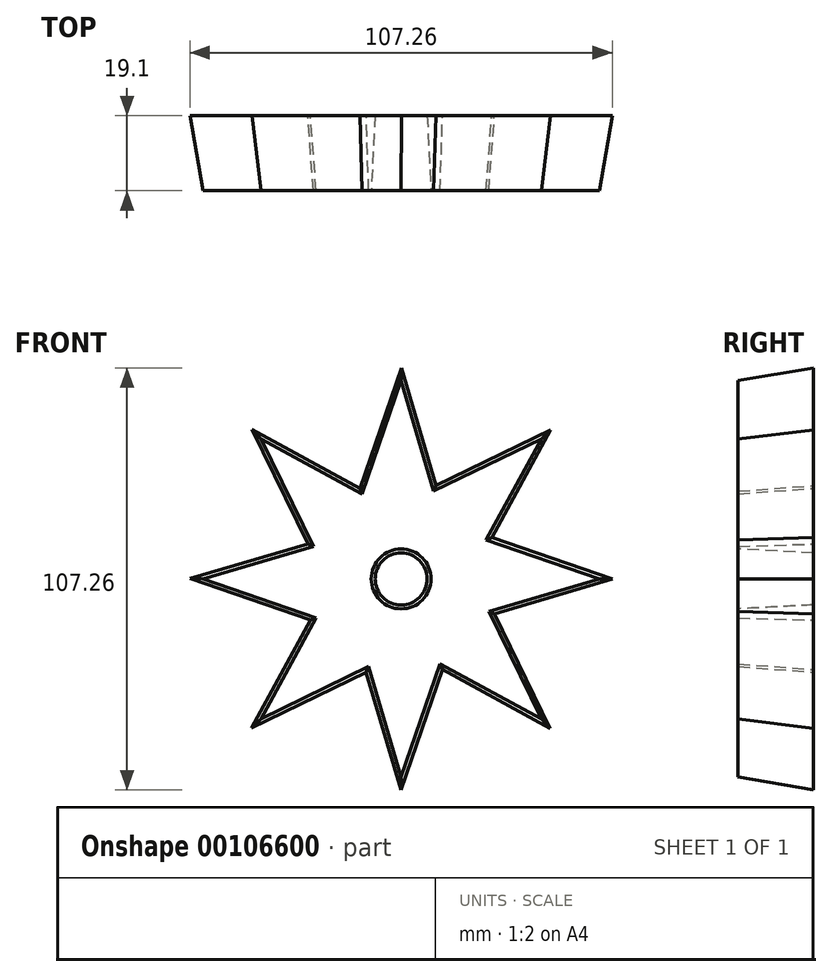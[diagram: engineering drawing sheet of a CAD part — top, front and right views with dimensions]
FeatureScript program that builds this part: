
annotation { "Feature Type Name" : "Feature", "Feature Type Description" : "" }
export const myFeature = defineFeature(function(context is Context, id is Id, definition is map)
    precondition{}
    {
        {
            var Q0;
            Q0=qCreatedBy(makeId("Front.planeOp"),FACE);
            var sketch = newSketch(context, id + "F0", { "sketchPlane" : qUnion([Q0])});
            skCircle(sketch, "E0", {"center": v(0, 0) * mm, "radius": 7.6 * mm});
            skCircle(sketch, "E1", {"center": v(0, 0) * mm, "radius": 19.27 * mm});
            skLineSegment(sketch, "E2.bottom", {"start": v(50.49, 50.34) * mm, "end": v(-50.49, 50.34) * mm});
            skLineSegment(sketch, "E2.top", {"start": v(50.49, -50.34) * mm, "end": v(-50.49, -50.34) * mm});
            skLineSegment(sketch, "E2.left", {"start": v(50.49, 50.34) * mm, "end": v(50.49, -50.34) * mm});
            skLineSegment(sketch, "E2.right", {"start": v(-50.49, 50.34) * mm, "end": v(-50.49, -50.34) * mm});
            skLineSegment(sketch, "E3", {"start": v(-12.24, 14.9) * mm, "end": v(0, 50.34) * mm});
            skLineSegment(sketch, "E4", {"start": v(9.95, 16.5) * mm, "end": v(0, 50.34) * mm});
            skLineSegment(sketch, "E5.1.0", {"start": v(-19.18, 1.88) * mm, "end": v(-35.6, 35.6) * mm});
            skLineSegment(sketch, "E5.1.1", {"start": v(-4.64, 18.7) * mm, "end": v(-35.6, 35.6) * mm});
            skLineSegment(sketch, "E5.2.0", {"start": v(-14.9, -12.24) * mm, "end": v(-50.34, 0) * mm});
            skLineSegment(sketch, "E5.2.1", {"start": v(-16.5, 9.95) * mm, "end": v(-50.34, 0) * mm});
            skLineSegment(sketch, "E5.3.0", {"start": v(-1.88, -19.18) * mm, "end": v(-35.6, -35.6) * mm});
            skLineSegment(sketch, "E5.3.1", {"start": v(-18.7, -4.64) * mm, "end": v(-35.6, -35.6) * mm});
            skLineSegment(sketch, "E5.4.0", {"start": v(12.24, -14.9) * mm, "end": v(0, -50.34) * mm});
            skLineSegment(sketch, "E5.4.1", {"start": v(-9.95, -16.5) * mm, "end": v(0, -50.34) * mm});
            skLineSegment(sketch, "E5.5.0", {"start": v(19.18, -1.88) * mm, "end": v(35.6, -35.6) * mm});
            skLineSegment(sketch, "E5.5.1", {"start": v(4.64, -18.7) * mm, "end": v(35.6, -35.6) * mm});
            skLineSegment(sketch, "E5.6.0", {"start": v(14.9, 12.24) * mm, "end": v(50.34, 0) * mm});
            skLineSegment(sketch, "E5.6.1", {"start": v(16.5, -9.95) * mm, "end": v(50.34, 0) * mm});
            skLineSegment(sketch, "E5.7.0", {"start": v(1.88, 19.18) * mm, "end": v(35.6, 35.6) * mm});
            skLineSegment(sketch, "E5.7.1", {"start": v(18.7, 4.64) * mm, "end": v(35.6, 35.6) * mm});
            skSolve(sketch);
        }
        {
            var Q0;
            {var subQ0=sQuery(id+"F0.wireOp",EDGE,"E5.1.1");var subQ1=sQuery(id+"F0.wireOp",EDGE,"E1");var subQ2=makeQuery(id+"F0.imprint","INTERSECT",VERTEX,{"derivedFrom":[subQ1,subQ0]});Q0=makeQuery(id+"F0.imprint","IMPRINT",FACE,{"disambiguationData":[TD([[makeQuery(id+"F0.imprint","IMPRINT",EDGE,{"disambiguationData":[TD([[subQ2,1.0]])],"derivedFrom":subQ1}),-1.0]])]});}
            var Q1;
            {var subQ5=sQuery(id+"F0.wireOp",EDGE,"E5.3.0");var subQ6=sQuery(id+"F0.wireOp",EDGE,"E1");var subQ7=makeQuery(id+"F0.imprint","INTERSECT",VERTEX,{"derivedFrom":[subQ6,subQ5]});Q1=makeQuery(id+"F0.imprint","IMPRINT",FACE,{"disambiguationData":[TD([[makeQuery(id+"F0.imprint","IMPRINT",EDGE,{"disambiguationData":[TD([[subQ7,-1.0]])],"derivedFrom":subQ6}),-1.0]])]});}
            var Q2;
            {var subQ0=sQuery(id+"F0.wireOp",EDGE,"E5.3.0");var subQ1=sQuery(id+"F0.wireOp",EDGE,"E1");var subQ2=makeQuery(id+"F0.imprint","INTERSECT",VERTEX,{"derivedFrom":[subQ1,subQ0]});Q2=makeQuery(id+"F0.imprint","IMPRINT",FACE,{"disambiguationData":[TD([[makeQuery(id+"F0.imprint","IMPRINT",EDGE,{"disambiguationData":[TD([[subQ2,1.0]])],"derivedFrom":subQ1}),-1.0]])]});}
            var Q3;
            {var subQ3=sQuery(id+"F0.wireOp",EDGE,"E5.5.0");var subQ5=sQuery(id+"F0.wireOp",EDGE,"E1");var subQ6=makeQuery(id+"F0.imprint","INTERSECT",VERTEX,{"derivedFrom":[subQ5,subQ3]});Q3=makeQuery(id+"F0.imprint","IMPRINT",FACE,{"disambiguationData":[TD([[makeQuery(id+"F0.imprint","IMPRINT",EDGE,{"disambiguationData":[TD([[subQ6,-1.0]])],"derivedFrom":subQ5}),-1.0]])]});}
            var Q4;
            {var subQ3=sQuery(id+"F0.wireOp",EDGE,"E5.4.0");var subQ5=sQuery(id+"F0.wireOp",EDGE,"E1");var subQ6=makeQuery(id+"F0.imprint","INTERSECT",VERTEX,{"derivedFrom":[subQ5,subQ3]});Q4=makeQuery(id+"F0.imprint","IMPRINT",FACE,{"disambiguationData":[TD([[makeQuery(id+"F0.imprint","IMPRINT",EDGE,{"disambiguationData":[TD([[subQ6,-1.0]])],"derivedFrom":subQ5}),-1.0]])]});}
            var Q5;
            {var subQ0=sQuery(id+"F0.wireOp",EDGE,"E5.6.0");var subQ1=sQuery(id+"F0.wireOp",EDGE,"E1");var subQ2=makeQuery(id+"F0.imprint","INTERSECT",VERTEX,{"derivedFrom":[subQ1,subQ0]});Q5=makeQuery(id+"F0.imprint","IMPRINT",FACE,{"disambiguationData":[TD([[makeQuery(id+"F0.imprint","IMPRINT",EDGE,{"disambiguationData":[TD([[subQ2,1.0]])],"derivedFrom":subQ1}),-1.0]])]});}
            var Q6;
            {var subQ0=sQuery(id+"F0.wireOp",EDGE,"E4");var subQ1=sQuery(id+"F0.wireOp",EDGE,"E1");var subQ2=makeQuery(id+"F0.imprint","INTERSECT",VERTEX,{"derivedFrom":[subQ1,subQ0]});Q6=makeQuery(id+"F0.imprint","IMPRINT",FACE,{"disambiguationData":[TD([[makeQuery(id+"F0.imprint","IMPRINT",EDGE,{"disambiguationData":[TD([[subQ2,-1.0]])],"derivedFrom":subQ1}),-1.0]])]});}
            var Q7;
            {var subQ0=sQuery(id+"F0.wireOp",EDGE,"E5.1.0");var subQ1=sQuery(id+"F0.wireOp",EDGE,"E1");var subQ2=makeQuery(id+"F0.imprint","INTERSECT",VERTEX,{"derivedFrom":[subQ1,subQ0]});Q7=makeQuery(id+"F0.imprint","IMPRINT",FACE,{"disambiguationData":[TD([[makeQuery(id+"F0.imprint","IMPRINT",EDGE,{"disambiguationData":[TD([[subQ2,1.0]])],"derivedFrom":subQ1}),-1.0]])]});}
            var Q8;
            {var subQ0=sQuery(id+"F0.wireOp",EDGE,"E3");var subQ1=sQuery(id+"F0.wireOp",EDGE,"E1");var subQ2=makeQuery(id+"F0.imprint","INTERSECT",VERTEX,{"derivedFrom":[subQ1,subQ0]});Q8=makeQuery(id+"F0.imprint","IMPRINT",FACE,{"disambiguationData":[TD([[makeQuery(id+"F0.imprint","IMPRINT",EDGE,{"disambiguationData":[TD([[subQ2,1.0]])],"derivedFrom":subQ1}),-1.0]])]});}
            var Q9;
            {var subQ0=sQuery(id+"F0.wireOp",EDGE,"E5.2.0");var subQ1=sQuery(id+"F0.wireOp",EDGE,"E1");var subQ2=makeQuery(id+"F0.imprint","INTERSECT",VERTEX,{"derivedFrom":[subQ1,subQ0]});Q9=makeQuery(id+"F0.imprint","IMPRINT",FACE,{"disambiguationData":[TD([[makeQuery(id+"F0.imprint","IMPRINT",EDGE,{"disambiguationData":[TD([[subQ2,1.0]])],"derivedFrom":subQ1}),-1.0]])]});}
            var Q10;
            {var subQ0=sQuery(id+"F0.wireOp",EDGE,"E5.4.0");var subQ1=sQuery(id+"F0.wireOp",EDGE,"E1");var subQ2=makeQuery(id+"F0.imprint","INTERSECT",VERTEX,{"derivedFrom":[subQ1,subQ0]});Q10=makeQuery(id+"F0.imprint","IMPRINT",FACE,{"disambiguationData":[TD([[makeQuery(id+"F0.imprint","IMPRINT",EDGE,{"disambiguationData":[TD([[subQ2,1.0]])],"derivedFrom":subQ1}),-1.0]])]});}
            var Q11;
            {var subQ0=sQuery(id+"F0.wireOp",EDGE,"E5.5.0");var subQ1=sQuery(id+"F0.wireOp",EDGE,"E1");var subQ2=makeQuery(id+"F0.imprint","INTERSECT",VERTEX,{"derivedFrom":[subQ1,subQ0]});Q11=makeQuery(id+"F0.imprint","IMPRINT",FACE,{"disambiguationData":[TD([[makeQuery(id+"F0.imprint","IMPRINT",EDGE,{"disambiguationData":[TD([[subQ2,1.0]])],"derivedFrom":subQ1}),-1.0]])]});}
            var Q12;
            {var subQ3=sQuery(id+"F0.wireOp",EDGE,"E4");var subQ6=sQuery(id+"F0.wireOp",EDGE,"E1");var subQ9=makeQuery(id+"F0.imprint","INTERSECT",VERTEX,{"derivedFrom":[subQ6,subQ3]});Q12=makeQuery(id+"F0.imprint","IMPRINT",FACE,{"disambiguationData":[TD([[makeQuery(id+"F0.imprint","IMPRINT",EDGE,{"disambiguationData":[TD([[subQ9,1.0]])],"derivedFrom":subQ6}),-1.0]])]});}
            var Q13;
            {var subQ3=sQuery(id+"F0.wireOp",EDGE,"E3");var subQ7=sQuery(id+"F0.wireOp",EDGE,"E1");var subQ8=makeQuery(id+"F0.imprint","INTERSECT",VERTEX,{"derivedFrom":[subQ7,subQ3]});Q13=makeQuery(id+"F0.imprint","IMPRINT",FACE,{"disambiguationData":[TD([[makeQuery(id+"F0.imprint","IMPRINT",EDGE,{"disambiguationData":[TD([[subQ8,-1.0]])],"derivedFrom":subQ7}),-1.0]])]});}
            var Q14;
            {var subQ3=sQuery(id+"F0.wireOp",EDGE,"E5.1.0");var subQ7=sQuery(id+"F0.wireOp",EDGE,"E1");var subQ8=makeQuery(id+"F0.imprint","INTERSECT",VERTEX,{"derivedFrom":[subQ7,subQ3]});Q14=makeQuery(id+"F0.imprint","IMPRINT",FACE,{"disambiguationData":[TD([[makeQuery(id+"F0.imprint","IMPRINT",EDGE,{"disambiguationData":[TD([[subQ8,-1.0]])],"derivedFrom":subQ7}),-1.0]])]});}
            var Q15;
            {var subQ3=sQuery(id+"F0.wireOp",EDGE,"E5.2.0");var subQ5=sQuery(id+"F0.wireOp",EDGE,"E1");var subQ6=makeQuery(id+"F0.imprint","INTERSECT",VERTEX,{"derivedFrom":[subQ5,subQ3]});Q15=makeQuery(id+"F0.imprint","IMPRINT",FACE,{"disambiguationData":[TD([[makeQuery(id+"F0.imprint","IMPRINT",EDGE,{"disambiguationData":[TD([[subQ6,-1.0]])],"derivedFrom":subQ5}),-1.0]])]});}
            var Q16;
            Q16=makeQuery(id+"F0.imprint","IMPRINT",FACE,{"disambiguationData":[TD([[makeQuery(id+"F0.imprint","IMPRINT",EDGE,{"derivedFrom":sQuery(id+"F0.wireOp",EDGE,"E0")}),-1.0]])]});
            extrude(context, id + "F1", {"entities" : qUnion([Q0, Q1, Q2, Q3, Q4, Q5, Q6, Q7, Q8, Q9, Q10, Q11, Q12, Q13, Q14, Q15, Q16]), "oppositeDirection" : true, "depth" : 19.1 * mm, "hasDraft" : true, "draftAngle" : 3 * degree});
        }
    });
